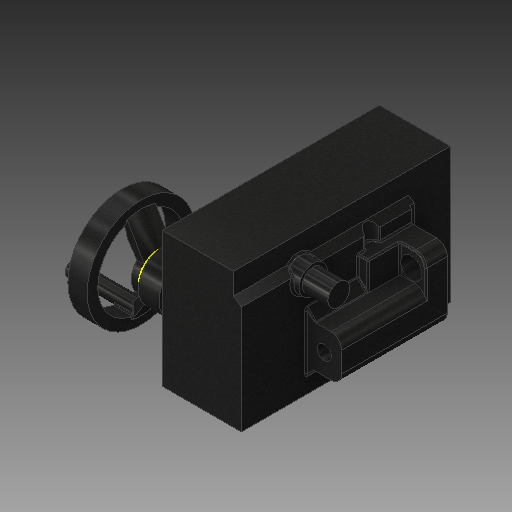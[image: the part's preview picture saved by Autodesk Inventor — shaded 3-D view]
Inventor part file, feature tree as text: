
AUTODESK INVENTOR PART (.ipt)
format: ipt  version: 2018 (Build 220112000, 112)  size: 647,168 bytes
history: native  units: in
note: dims shown in document units (in); Inventor stores cm internally (conversion verified against a paired STEP export)
features: sketch x20, extrude x16, fillet x6, plane x3, loft x2, projected_geometry x2, chamfer x1, other x1
ambient origin geometry x8: Origin, YZ Plane, XZ Plane, XY Plane, X Axis, Y Axis, Z Axis, Center Point
bodies: Solid1 (feature_tree)
feature tree (51):
  extrude  "Extrusion1"  Depth=4.3701in
  extrude  "Extrusion2"  Depth=1.1811in
  extrude  "Extrusion3"  Depth=12.0079in TaperAngle=0.0deg
  extrude  "Extrusion4"  Depth=12.0079in TaperAngle=0.0deg
  extrude  "Extrusion5"  Depth=1.9685in
  extrude  "Extrusion6"  Depth=1.4567in TaperAngle=0.0deg
  extrude  "Extrusion7"  Depth=4.6457in TaperAngle=0.0deg
  fillet  "Fillet2"  Radius=1.7717in
  chamfer  "Chamfer1"  Distance=0.5512in
  fillet  "Fillet3"  Radius=0.7874in
  extrude  "Extrusion8"  Depth=0.5118in TaperAngle=0.0deg
  extrude  "Extrusion9"  Depth=0.315in
  extrude  "Extrusion10"  Depth=0.2559in TaperAngle=0.0deg
  fillet  "Fillet4"  Radius=0.5906in
  extrude  "Extrusion11"  Depth=0.0787in
  extrude  "Extrusion12"  Depth=0.0787in
  sketch  "Sketch14"  dims[d39=0.9449in d40=0.7874in]
  plane  "Work Plane2"
  loft  "Loft1"
  plane  "Work Plane3"
  extrude  "Extrusion13"  Depth=1.1417in
  extrude  "Extrusion15"  Depth=1.7717in
  plane  "Work Plane5"
  sketch  "Sketch22"  dims[d55=3.3071in d56=1.1811in]
  sketch  "Sketch16"  dims[d43=0.2559in d44=0.0in d45=1.7717in]
  loft  "Loft2"
  fillet  "Fillet5"  Radius=0.8268in
  extrude  "Extrusion16"  Depth=1.4173in TaperAngle=0.0deg
  fillet  "Fillet6"  Radius=0.1181in
  fillet  "Fillet7"  Radius=2.7559in
  extrude  "Extrusion17"  Depth=1.1811in
  sketch  "Sketch1"  dims[d0=3.937in d1=4.3701in]
  sketch  "Sketch2"  dims[d2=7.4803in d3=1.1811in]
  sketch  "Sketch3"  dims[d4=5.9843in d5=12.0079in d6=0.0in]
  sketch  "Sketch4"  dims[d7=2.3228in d8=12.0079in d9=0.0in]
  sketch  "Sketch5"  dims[d10=0.7087in d11=1.9685in]
  sketch  "Sketch6"  dims[d12=3.8976in d13=1.4567in d14=0.0in]
  sketch  "Sketch7"  dims[d15=1.5748in d16=4.6457in d17=0.0in d18=1.7717in d19=0.5512in d20=0.0in d21=0.7874in]
  sketch  "Sketch9"  dims[d22=0.7874in d23=0.5118in d24=0.0in]
  sketch  "Sketch10"  dims[d25=2.3622in d26=0.315in]
  sketch  "Sketch11"  dims[d27=0.5906in d28=0.2559in d29=0.0in d31=0.5906in]
  sketch  "Sketch12"  dims[d32=0.5118in d33=0.0787in d34=45.0deg d36=1.1811in]
  sketch  "Sketch13"  dims[d37=1.6142in d38=0.0787in]
  projected_geometry  "Projected Loop1"
  sketch  "Sketch15"  dims[d41=0.9646in d42=1.1417in]
  other  "Edges1"
  sketch  "Sketch18"  dims[d46=1.5748in d47=3.5827in d48=0.8268in d49=0.0in]
  sketch  "Sketch21"  dims[d50=1.2205in d51=1.4173in d52=0.0in d53=0.1181in d54=2.7559in]
  projected_geometry  "Projected Loop4"
  sketch  "Sketch23"  dims[d57=1.1417in d58=0.0in]
  sketch  "Sketch24"  dims[d59=2.2047in d60=0.2756in d61=0.0in d62=0.9449in d63=5.1181in d64=0.0in d65=90.0deg d66=0.0in d67=90.0deg d68=0.6693in d69=2.2047in d71=0.0in d72=90.0deg d75=2.2047in d76=4.7244in d78=0.7874in d79=0.5118in d80=0.2756in d81=0.0in d82=2.7559in d87=5.9843in d88=4.8031in d89=1.063in d90=0.0in d91=1.7717in d92=0.0in d93=90.0deg d94=0.5906in d95=0.7874in d96=2.2047in d97=1.063in d98=0.0in d99=0.0787in d100=0.0787in d101=2.7559in d102=0.0in]
